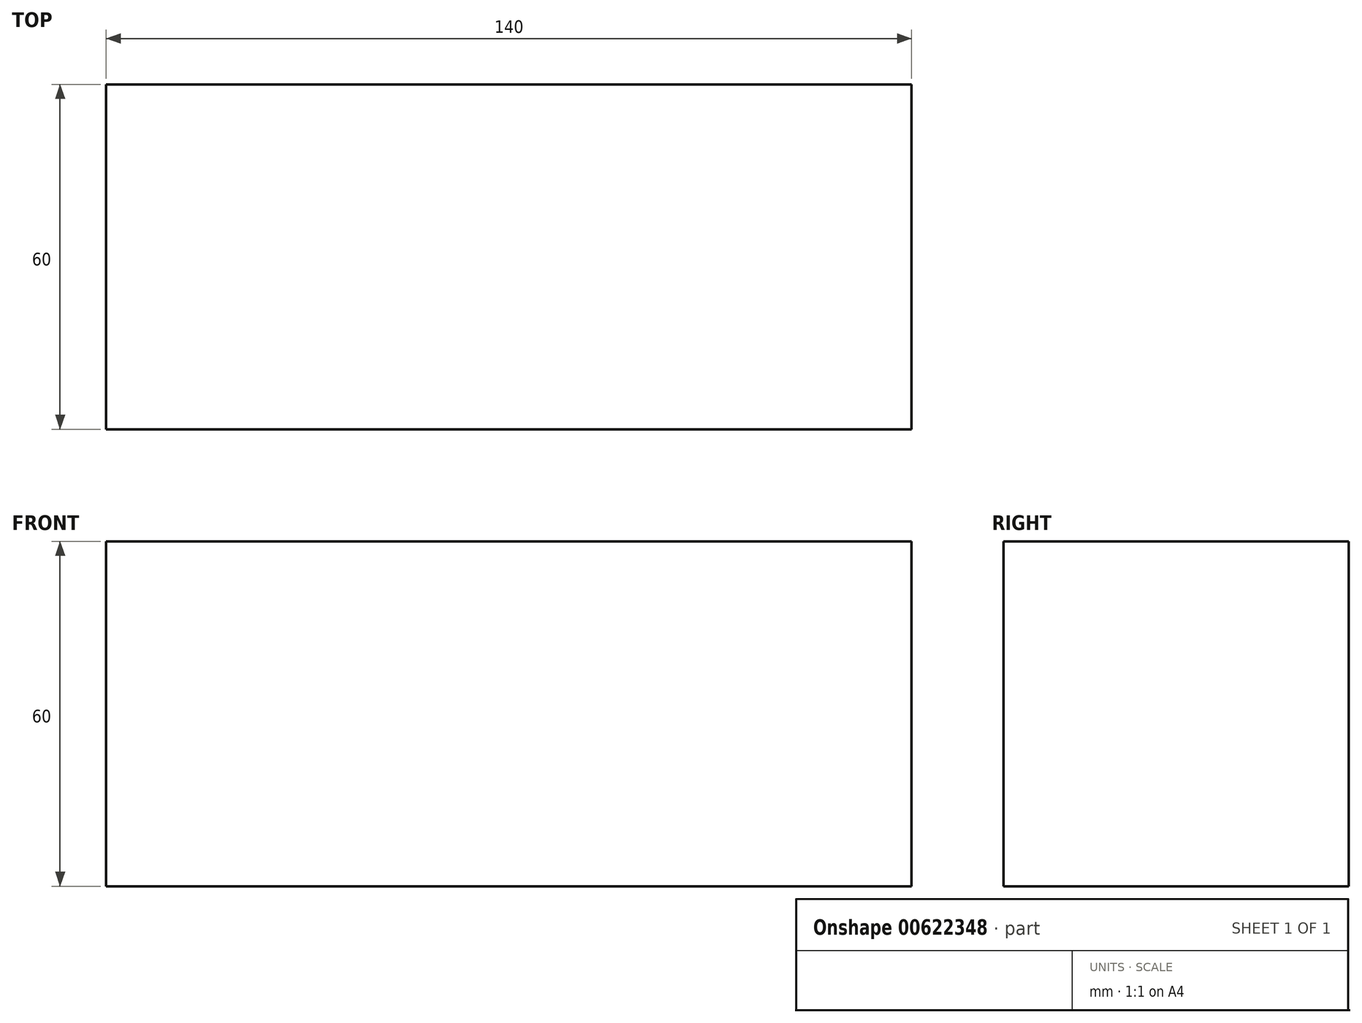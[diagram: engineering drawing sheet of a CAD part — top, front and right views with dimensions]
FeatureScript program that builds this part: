
annotation { "Feature Type Name" : "Feature", "Feature Type Description" : "" }
export const myFeature = defineFeature(function(context is Context, id is Id, definition is map)
    precondition{}
    {
        {
            var Q0;
            Q0=qCreatedBy(makeId("Top.planeOp"),FACE);
            var sketch = newSketch(context, id + "F0", { "sketchPlane" : qUnion([Q0])});
            skLineSegment(sketch, "E0.bottom", {"start": v(-1778, -426.5) * mm, "end": v(1778, -426.5) * mm});
            skLineSegment(sketch, "E0.top", {"start": v(-1778, 426.5) * mm, "end": v(1778, 426.5) * mm});
            skLineSegment(sketch, "E0.left", {"start": v(-1778, -426.5) * mm, "end": v(-1778, 426.5) * mm});
            skLineSegment(sketch, "E0.right", {"start": v(1778, -426.5) * mm, "end": v(1778, 426.5) * mm});
            skPoint(sketch, "E0.middle", {"position": v(0, 0) * mm});
            skLineSegment(sketch, "E1.bottom", {"start": v(-70, -30) * mm, "end": v(70, -30) * mm});
            skLineSegment(sketch, "E1.top", {"start": v(-70, 30) * mm, "end": v(70, 30) * mm});
            skLineSegment(sketch, "E1.left", {"start": v(-70, -30) * mm, "end": v(-70, 30) * mm});
            skLineSegment(sketch, "E1.right", {"start": v(70, -30) * mm, "end": v(70, 30) * mm});
            skSolve(sketch);
        }
        {
            var Q0;
            Q0=makeQuery(id+"F0.imprint","IMPRINT",FACE,{"disambiguationData":[TD([[makeQuery(id+"F0.imprint","IMPRINT",EDGE,{"derivedFrom":sQuery(id+"F0.wireOp",EDGE,"E1.bottom")}),1.0]])]});
            extrude(context, id + "F1", {"entities" : qUnion([Q0]), "depth" : 60 * mm, "offsetDistance" : 25 * mm});
        }
        {
            var Q0;
            Q0=makeQuery(id+"F1.opExtrude","CAP_FACE",FACE,{"disambiguationData":[OSD([sQuery(id+"F0.wireOp",EDGE,"E1.bottom"),sQuery(id+"F0.wireOp",EDGE,"E1.top"),sQuery(id+"F0.wireOp",EDGE,"E1.left"),sQuery(id+"F0.wireOp",EDGE,"E1.right")])],"isStart":false});
            var sketch = newSketch(context, id + "F2", { "sketchPlane" : qUnion([Q0])});
            skCircle(sketch, "E2", {"center": v(0, 0) * mm, "radius": 10.08 * mm});
            skSolve(sketch);
        }
        {
            var Q0;
            Q0=makeQuery(id+"F2.imprint","IMPRINT",FACE,{"disambiguationData":[TD([[makeQuery(id+"F2.imprint","IMPRINT",EDGE,{"derivedFrom":sQuery(id+"F2.wireOp",EDGE,"E2")}),1.0]])]});
            extrude(context, id + "F3", {"entities" : qUnion([Q0]), "operationType" : NewBodyOperationType.REMOVE, "depth" : 18 * mm, "offsetDistance" : 25 * mm});
        }
    });
